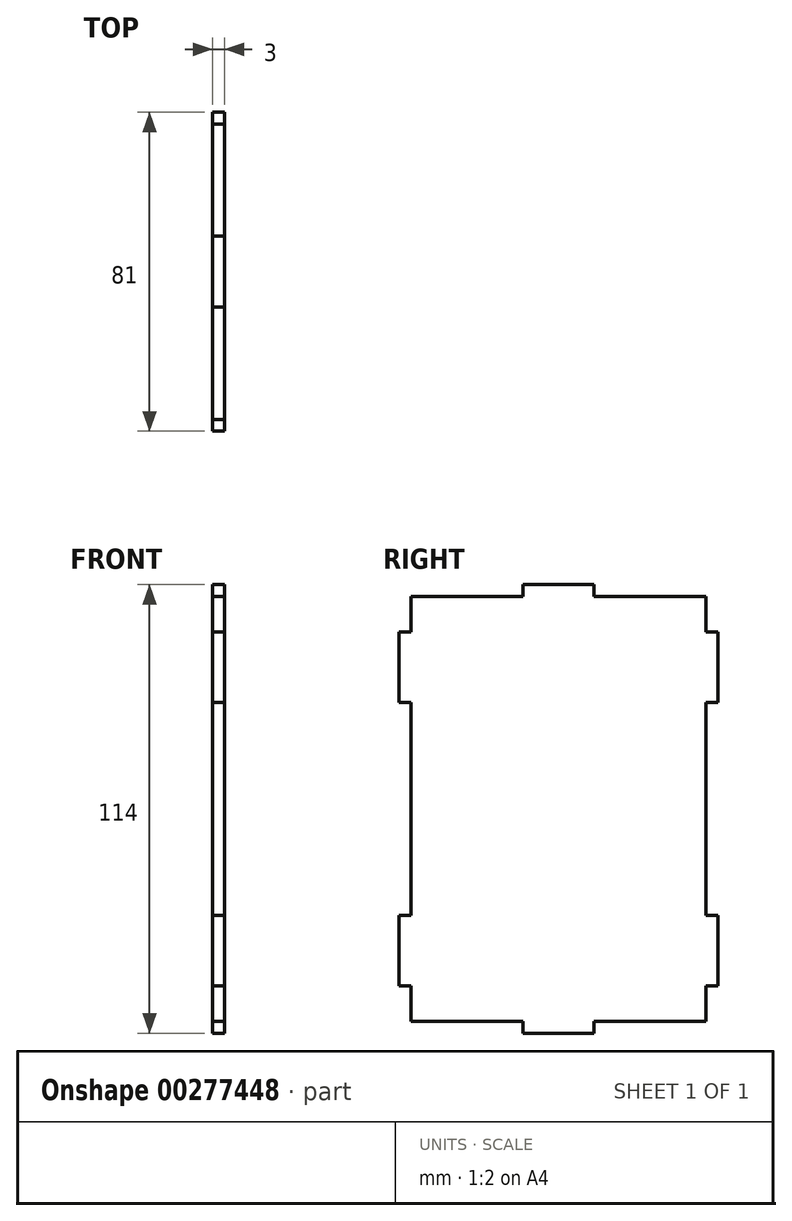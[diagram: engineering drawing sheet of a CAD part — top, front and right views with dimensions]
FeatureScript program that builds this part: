
annotation { "Feature Type Name" : "Feature", "Feature Type Description" : "" }
export const myFeature = defineFeature(function(context is Context, id is Id, definition is map)
    precondition{}
    {
        {
            var Q0;
            Q0=qCreatedBy(makeId("Right.planeOp"),FACE);
            var sketch = newSketch(context, id + "F0", { "sketchPlane" : qUnion([Q0])});
            skLineSegment(sketch, "E0.bottom", {"start": v(37.5, 54) * mm, "end": v(9, 54) * mm});
            skLineSegment(sketch, "E0.top", {"start": v(37.5, -54) * mm, "end": v(9, -54) * mm});
            skLineSegment(sketch, "E0.left", {"start": v(37.5, 54) * mm, "end": v(37.5, 45) * mm});
            skLineSegment(sketch, "E0.right", {"start": v(-37.5, 54) * mm, "end": v(-37.5, 45) * mm});
            skPoint(sketch, "E0.middle", {"position": v(0, 0) * mm});
            skLineSegment(sketch, "E1.bottom", {"start": v(37.5, 45) * mm, "end": v(40.5, 45) * mm});
            skLineSegment(sketch, "E1.top", {"start": v(37.5, 27) * mm, "end": v(40.5, 27) * mm});
            skLineSegment(sketch, "E1.right", {"start": v(40.5, 45) * mm, "end": v(40.5, 27) * mm});
            skLineSegment(sketch, "E2.bottom", {"start": v(37.5, -27) * mm, "end": v(40.5, -27) * mm});
            skLineSegment(sketch, "E2.top", {"start": v(37.5, -45) * mm, "end": v(40.5, -45) * mm});
            skLineSegment(sketch, "E2.right", {"start": v(40.5, -27) * mm, "end": v(40.5, -45) * mm});
            skLineSegment(sketch, "E3.bottom", {"start": v(-37.5, 45) * mm, "end": v(-40.5, 45) * mm});
            skLineSegment(sketch, "E3.top", {"start": v(-37.5, 27) * mm, "end": v(-40.5, 27) * mm});
            skLineSegment(sketch, "E3.right", {"start": v(-40.5, 45) * mm, "end": v(-40.5, 27) * mm});
            skLineSegment(sketch, "E4.bottom", {"start": v(-37.5, -27) * mm, "end": v(-40.5, -27) * mm});
            skLineSegment(sketch, "E4.top", {"start": v(-37.5, -45) * mm, "end": v(-40.5, -45) * mm});
            skLineSegment(sketch, "E4.right", {"start": v(-40.5, -27) * mm, "end": v(-40.5, -45) * mm});
            skLineSegment(sketch, "E5.top", {"start": v(-9, 57) * mm, "end": v(9, 57) * mm});
            skLineSegment(sketch, "E5.left", {"start": v(-9, 54) * mm, "end": v(-9, 57) * mm});
            skLineSegment(sketch, "E5.right", {"start": v(9, 54) * mm, "end": v(9, 57) * mm});
            skLineSegment(sketch, "E6.top", {"start": v(-9, -57) * mm, "end": v(9, -57) * mm});
            skLineSegment(sketch, "E6.left", {"start": v(-9, -54) * mm, "end": v(-9, -57) * mm});
            skLineSegment(sketch, "E6.right", {"start": v(9, -54) * mm, "end": v(9, -57) * mm});
            skLineSegment(sketch, "E7.trimOffspring", {"start": v(-9, 54) * mm, "end": v(-37.5, 54) * mm});
            skLineSegment(sketch, "E8.trimOffspring", {"start": v(37.5, 27) * mm, "end": v(37.5, -27) * mm});
            skLineSegment(sketch, "E9.trimOffspring", {"start": v(-37.5, 27) * mm, "end": v(-37.5, -27) * mm});
            skLineSegment(sketch, "E10.trimOffspring", {"start": v(37.5, -45) * mm, "end": v(37.5, -54) * mm});
            skLineSegment(sketch, "E11.trimOffspring", {"start": v(-37.5, -45) * mm, "end": v(-37.5, -54) * mm});
            skLineSegment(sketch, "E12.trimOffspring", {"start": v(-9, -54) * mm, "end": v(-37.5, -54) * mm});
            skLineSegment(sketch, "E13", {"start": v(0, 0) * mm, "end": v(17.02, 0) * mm, "construction": true});
            skLineSegment(sketch, "E14", {"start": v(0, 0) * mm, "end": v(0, 15.14) * mm, "construction": true});
            skSolve(sketch);
        }
        {
            var Q0;
            Q0=makeQuery(id+"F0.imprint","IMPRINT",FACE,{"disambiguationData":[TD([[makeQuery(id+"F0.imprint","IMPRINT",EDGE,{"derivedFrom":sQuery(id+"F0.wireOp",EDGE,"E0.bottom")}),1.0]])]});
            extrude(context, id + "F1", {"entities" : qUnion([Q0]), "depth" : 3 * mm});
        }
    });
